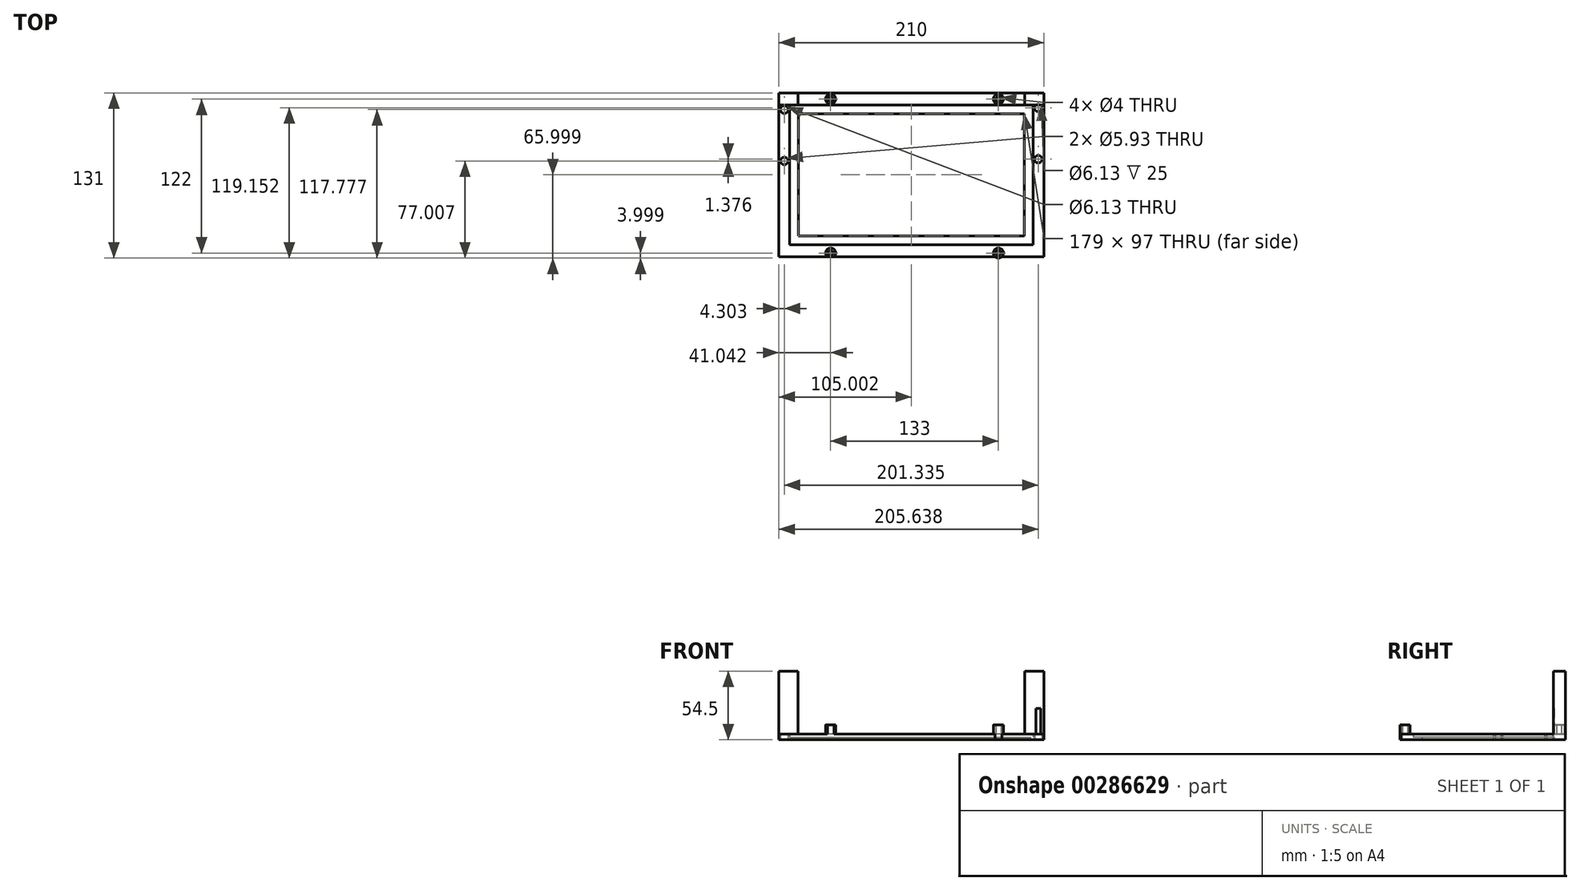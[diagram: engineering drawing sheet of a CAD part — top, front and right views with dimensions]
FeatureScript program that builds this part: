
annotation { "Feature Type Name" : "Feature", "Feature Type Description" : "" }
export const myFeature = defineFeature(function(context is Context, id is Id, definition is map)
    precondition{}
    {
        {
            var Q0;
            Q0=qCreatedBy(makeId("Top.planeOp"),FACE);
            var sketch = newSketch(context, id + "F0", { "sketchPlane" : qUnion([Q0])});
            skLineSegment(sketch, "E0.bottom", {"start": v(-66.79, 80.24) * mm, "end": v(143.21, 80.24) * mm});
            skLineSegment(sketch, "E0.top", {"start": v(-66.79, -49.76) * mm, "end": v(143.21, -49.76) * mm});
            skLineSegment(sketch, "E0.left", {"start": v(-66.79, 80.24) * mm, "end": v(-66.79, -49.76) * mm});
            skLineSegment(sketch, "E0.right", {"start": v(143.21, 80.24) * mm, "end": v(143.21, -49.76) * mm});
            skLineSegment(sketch, "E1.bottom", {"start": v(-58.29, 70.74) * mm, "end": v(134.71, 70.74) * mm});
            skLineSegment(sketch, "E1.top", {"start": v(-58.29, -40.26) * mm, "end": v(134.71, -40.26) * mm});
            skLineSegment(sketch, "E1.left", {"start": v(-58.29, 70.74) * mm, "end": v(-58.29, -40.26) * mm});
            skLineSegment(sketch, "E1.right", {"start": v(134.71, 70.74) * mm, "end": v(134.71, -40.26) * mm});
            skLineSegment(sketch, "E2.bottom", {"start": v(-51.29, 63.74) * mm, "end": v(127.71, 63.74) * mm});
            skLineSegment(sketch, "E2.top", {"start": v(-51.29, -33.26) * mm, "end": v(127.71, -33.26) * mm});
            skLineSegment(sketch, "E2.left", {"start": v(-51.29, 63.74) * mm, "end": v(-51.29, -33.26) * mm});
            skLineSegment(sketch, "E2.right", {"start": v(127.71, 63.74) * mm, "end": v(127.71, -33.26) * mm});
            skCircle(sketch, "E3", {"center": v(-25.75, 75.24) * mm, "radius": 2 * mm});
            skCircle(sketch, "E4.0.1.0", {"center": v(-25.75, -46.76) * mm, "radius": 2 * mm});
            skCircle(sketch, "E4.1.0.0", {"center": v(107.25, 75.24) * mm, "radius": 2 * mm});
            skCircle(sketch, "E4.1.1.0", {"center": v(107.25, -46.76) * mm, "radius": 2 * mm});
            skLineSegment(sketch, "E4.direction1", {"start": v(-25.75, 75.24) * mm, "end": v(107.25, 75.24) * mm, "construction": true});
            skLineSegment(sketch, "E4.direction2", {"start": v(-25.75, 75.24) * mm, "end": v(-25.75, -46.76) * mm, "construction": true});
            skCircle(sketch, "E5", {"center": v(-25.75, 75.24) * mm, "radius": 4 * mm});
            skCircle(sketch, "E6.0.1.0", {"center": v(-25.75, -46.76) * mm, "radius": 4 * mm});
            skCircle(sketch, "E6.1.0.0", {"center": v(107.25, 75.24) * mm, "radius": 4 * mm});
            skCircle(sketch, "E6.1.1.0", {"center": v(107.25, -46.76) * mm, "radius": 4 * mm});
            skSolve(sketch);
        }
        {
            var Q0;
            Q0=makeQuery(id+"F0.imprint","IMPRINT",FACE,{"disambiguationData":[TD([[makeQuery(id+"F0.imprint","IMPRINT",EDGE,{"derivedFrom":sQuery(id+"F0.wireOp",EDGE,"E1.top")}),1.0]])]});
            extrude(context, id + "F1", {"entities" : qUnion([Q0]), "depth" : 2 * mm});
        }
        {
            var Q0;
            Q0=makeQuery(id+"F0.imprint","IMPRINT",FACE,{"disambiguationData":[TD([[makeQuery(id+"F0.imprint","IMPRINT",EDGE,{"derivedFrom":sQuery(id+"F0.wireOp",EDGE,"E3")}),-1.0]])]});
            var Q1;
            Q1=makeQuery(id+"F0.imprint","IMPRINT",FACE,{"disambiguationData":[TD([[makeQuery(id+"F0.imprint","IMPRINT",EDGE,{"derivedFrom":sQuery(id+"F0.wireOp",EDGE,"E4.1.0.0")}),-1.0]])]});
            var Q2;
            Q2=makeQuery(id+"F0.imprint","IMPRINT",FACE,{"disambiguationData":[TD([[makeQuery(id+"F0.imprint","IMPRINT",EDGE,{"derivedFrom":sQuery(id+"F0.wireOp",EDGE,"E4.0.1.0")}),-1.0]])]});
            var Q3;
            Q3=makeQuery(id+"F0.imprint","IMPRINT",FACE,{"disambiguationData":[TD([[makeQuery(id+"F0.imprint","IMPRINT",EDGE,{"derivedFrom":sQuery(id+"F0.wireOp",EDGE,"E4.1.1.0")}),-1.0]])]});
            var Q4;
            Q4=makeQuery(id+"F0.imprint","IMPRINT",FACE,{"disambiguationData":[TD([[makeQuery(id+"F0.imprint","IMPRINT",EDGE,{"derivedFrom":sQuery(id+"F0.wireOp",EDGE,"E0.bottom")}),-1.0]])]});
            extrude(context, id + "F2", {"entities" : qUnion([Q0, Q1, Q2, Q3, Q4]), "operationType" : NewBodyOperationType.ADD, "depth" : 4.5 * mm});
        }
        {
            var Q0;
            Q0=makeQuery(id+"F0.imprint","IMPRINT",FACE,{"disambiguationData":[TD([[makeQuery(id+"F0.imprint","IMPRINT",EDGE,{"derivedFrom":sQuery(id+"F0.wireOp",EDGE,"E3")}),1.0]])]});
            var Q1;
            Q1=makeQuery(id+"F0.imprint","IMPRINT",FACE,{"disambiguationData":[TD([[makeQuery(id+"F0.imprint","IMPRINT",EDGE,{"derivedFrom":sQuery(id+"F0.wireOp",EDGE,"E4.1.0.0")}),1.0]])]});
            var Q2;
            Q2=makeQuery(id+"F0.imprint","IMPRINT",FACE,{"disambiguationData":[TD([[makeQuery(id+"F0.imprint","IMPRINT",EDGE,{"derivedFrom":sQuery(id+"F0.wireOp",EDGE,"E4.1.1.0")}),1.0]])]});
            var Q3;
            Q3=makeQuery(id+"F0.imprint","IMPRINT",FACE,{"disambiguationData":[TD([[makeQuery(id+"F0.imprint","IMPRINT",EDGE,{"derivedFrom":sQuery(id+"F0.wireOp",EDGE,"E4.0.1.0")}),1.0]])]});
            extrude(context, id + "F3", {"entities" : qUnion([Q0, Q1, Q2, Q3]), "operationType" : NewBodyOperationType.REMOVE, "oppositeDirection" : true, "depth" : 5 * mm});
        }
        {
            var Q0;
            Q0=makeQuery(id+"F0.imprint","IMPRINT",FACE,{"disambiguationData":[TD([[makeQuery(id+"F0.imprint","IMPRINT",EDGE,{"derivedFrom":sQuery(id+"F0.wireOp",EDGE,"E3")}),-1.0]])]});
            var Q1;
            Q1=makeQuery(id+"F0.imprint","IMPRINT",FACE,{"disambiguationData":[TD([[makeQuery(id+"F0.imprint","IMPRINT",EDGE,{"derivedFrom":sQuery(id+"F0.wireOp",EDGE,"E4.1.1.0")}),-1.0]])]});
            var Q2;
            {var subQ0=sQuery(id+"F0.wireOp",EDGE,"E6.1.1.0");var subQ1=sQuery(id+"F0.wireOp",EDGE,"E0.top");var subQ2=makeQuery(id+"F0.imprint","INTERSECT",VERTEX,{"disambiguationData":[OD(0.0)],"derivedFrom":[subQ1,subQ0]});Q2=makeQuery(id+"F0.imprint","IMPRINT",FACE,{"disambiguationData":[TD([[makeQuery(id+"F0.imprint","IMPRINT",EDGE,{"disambiguationData":[TD([[subQ2,-1.0]])],"derivedFrom":subQ1}),-1.0]])]});}
            var Q3;
            Q3=makeQuery(id+"F0.imprint","IMPRINT",FACE,{"disambiguationData":[TD([[makeQuery(id+"F0.imprint","IMPRINT",EDGE,{"derivedFrom":sQuery(id+"F0.wireOp",EDGE,"E4.0.1.0")}),-1.0]])]});
            var Q4;
            {var subQ0=sQuery(id+"F0.wireOp",EDGE,"E6.0.1.0");var subQ1=sQuery(id+"F0.wireOp",EDGE,"E0.top");var subQ2=makeQuery(id+"F0.imprint","INTERSECT",VERTEX,{"disambiguationData":[OD(0.0)],"derivedFrom":[subQ1,subQ0]});Q4=makeQuery(id+"F0.imprint","IMPRINT",FACE,{"disambiguationData":[TD([[makeQuery(id+"F0.imprint","IMPRINT",EDGE,{"disambiguationData":[TD([[subQ2,-1.0]])],"derivedFrom":subQ1}),-1.0]])]});}
            var Q5;
            Q5=makeQuery(id+"F0.imprint","IMPRINT",FACE,{"disambiguationData":[TD([[makeQuery(id+"F0.imprint","IMPRINT",EDGE,{"derivedFrom":sQuery(id+"F0.wireOp",EDGE,"E4.1.0.0")}),-1.0]])]});
            extrude(context, id + "F4", {"entities" : qUnion([Q0, Q1, Q2, Q3, Q4, Q5]), "operationType" : NewBodyOperationType.ADD, "depth" : 11.85 * mm});
        }
        {
            var Q0;
            Q0=makeQuery(id+"F2.opExtrude","CAP_FACE",FACE,{"disambiguationData":[OSD([sQuery(id+"F0.wireOp",EDGE,"E0.bottom"),sQuery(id+"F0.wireOp",EDGE,"E0.top"),sQuery(id+"F0.wireOp",EDGE,"E0.left"),sQuery(id+"F0.wireOp",EDGE,"E0.right"),sQuery(id+"F0.wireOp",EDGE,"E1.bottom"),sQuery(id+"F0.wireOp",EDGE,"E1.top"),sQuery(id+"F0.wireOp",EDGE,"E1.left"),sQuery(id+"F0.wireOp",EDGE,"E1.right"),sQuery(id+"F0.wireOp",EDGE,"E3"),sQuery(id+"F0.wireOp",EDGE,"E4.0.1.0"),sQuery(id+"F0.wireOp",EDGE,"E4.1.0.0"),sQuery(id+"F0.wireOp",EDGE,"E4.1.1.0")])],"isStart":false});
            var sketch = newSketch(context, id + "F5", { "sketchPlane" : qUnion([Q0])});
            skLineSegment(sketch, "E7", {"start": v(-58.29, 70.74) * mm, "end": v(-66.79, 70.74) * mm});
            skLineSegment(sketch, "E8", {"start": v(-66.79, 70.74) * mm, "end": v(-66.79, 80.24) * mm});
            skLineSegment(sketch, "E9", {"start": v(-66.79, 80.24) * mm, "end": v(-51.73, 80.24) * mm});
            skLineSegment(sketch, "E10", {"start": v(-51.73, 80.24) * mm, "end": v(-51.73, 70.74) * mm});
            skLineSegment(sketch, "E11", {"start": v(-51.73, 70.74) * mm, "end": v(-58.29, 70.74) * mm});
            skLineSegment(sketch, "E12", {"start": v(134.71, 70.74) * mm, "end": v(143.21, 70.74) * mm});
            skLineSegment(sketch, "E13", {"start": v(143.21, 70.74) * mm, "end": v(143.21, 80.24) * mm});
            skLineSegment(sketch, "E14", {"start": v(143.21, 80.24) * mm, "end": v(128.08, 80.24) * mm});
            skLineSegment(sketch, "E15", {"start": v(128.08, 80.24) * mm, "end": v(128.08, 70.74) * mm});
            skLineSegment(sketch, "E16", {"start": v(128.08, 70.74) * mm, "end": v(134.71, 70.74) * mm});
            skSolve(sketch);
        }
        {
            var Q0;
            Q0=makeQuery(id+"F5.imprint","IMPRINT",FACE,{"disambiguationData":[TD([[makeQuery(id+"F5.imprint","IMPRINT",EDGE,{"derivedFrom":sQuery(id+"F5.wireOp",EDGE,"E12")}),1.0]])]});
            var Q1;
            Q1=makeQuery(id+"F5.imprint","IMPRINT",FACE,{"disambiguationData":[TD([[makeQuery(id+"F5.imprint","IMPRINT",EDGE,{"derivedFrom":sQuery(id+"F5.wireOp",EDGE,"E7")}),-1.0]])]});
            extrude(context, id + "F6", {"entities" : qUnion([Q0, Q1]), "operationType" : NewBodyOperationType.ADD, "depth" : 50 * mm});
        }
        {
            var Q0;
            Q0=makeQuery(id+"F0.imprint","IMPRINT",FACE,{"disambiguationData":[TD([[makeQuery(id+"F0.imprint","IMPRINT",EDGE,{"derivedFrom":sQuery(id+"F0.wireOp",EDGE,"E0.bottom")}),-1.0]])]});
            var sketch = newSketch(context, id + "F7", { "sketchPlane" : qUnion([Q0])});
            skSolve(sketch);
        }
        {
            var Q0;
            Q0=makeQuery(id+"F7.imprint","IMPRINT",FACE,{"disambiguationData":[TD([[makeQuery(id+"F7.imprint","IMPRINT",EDGE,{"derivedFrom":makeQuery(id+"F0.imprint","IMPRINT",EDGE,{"derivedFrom":sQuery(id+"F0.wireOp",EDGE,"E0.bottom")})}),-1.0]])]});
            var sketch = newSketch(context, id + "F8", { "sketchPlane" : qUnion([Q0])});
            skLineSegment(sketch, "E17", {"start": v(134.57, 68.4) * mm, "end": v(143.13, 68.4) * mm});
            skLineSegment(sketch, "E18", {"start": v(138.85, 68.4) * mm, "end": v(138.85, 27.62) * mm});
            skLineSegment(sketch, "E19", {"start": v(140.93, 27.62) * mm, "end": v(138.85, 27.62) * mm});
            skLineSegment(sketch, "E20", {"start": v(140.93, 27.62) * mm, "end": v(150.16, 27.62) * mm});
            skCircle(sketch, "E21", {"center": v(138.85, 27.62) * mm, "radius": 2.96 * mm});
            skCircle(sketch, "E22", {"center": v(138.85, 68.4) * mm, "radius": 3.06 * mm});
            skLineSegment(sketch, "E23", {"start": v(-66.77, 67.02) * mm, "end": v(-58.2, 67.02) * mm});
            skLineSegment(sketch, "E24", {"start": v(-62.49, 67.02) * mm, "end": v(-62.49, 26.25) * mm});
            skLineSegment(sketch, "E25", {"start": v(-66.77, 26.25) * mm, "end": v(-57.53, 26.25) * mm});
            skCircle(sketch, "E26", {"center": v(-62.49, 26.25) * mm, "radius": 2.96 * mm});
            skCircle(sketch, "E27", {"center": v(-62.49, 67.02) * mm, "radius": 3.06 * mm});
            skSolve(sketch);
        }
        {
            var Q0;
            Q0 = qSketchRegion(id + "F8", true);
            var Q1;
            Q1=sQuery(id+"F8.wireOp",EDGE,"E26");
            var Q2;
            Q2=sQuery(id+"F8.wireOp",EDGE,"E27");
            var Q3;
            Q3=sQuery(id+"F8.wireOp",EDGE,"E22");
            var Q4;
            Q4=sQuery(id+"F8.wireOp",EDGE,"E21");
            extrude(context, id + "F9", {"entities" : qUnion([Q0]), "operationType" : NewBodyOperationType.REMOVE, "surfaceEntities" : qUnion([Q1, Q2, Q3, Q4]), "depth" : 25 * mm});
        }
    });
